# Revit family: 2Incepa_Boss_Bacia com Caixa Acoplar_89351
name_source: partatom
category: Plumbing Fixtures
revit_build: Autodesk Revit MEP 2014 (Build: 20131024_2115(x64)
units: mm (PartAtom-declared; Revit-internal decimal feet)

## types (2) — shared parameters
Assembly Code = D2010100
CWFU = 1
Description = Bacia com caixa acoplada cor branca (89351) 365 x 640 mm, linha Boss - Louças Incepa
Desenvolvido por = ofcdesk
Diâmetro Ponto de Esgoto = 100 mm
Incepa: Categoria = Linha Boss
Incepa: Cores Disponíveis = Branco
Incepa: Código = 89351
Incepa: Descrição = Bacia com caixa acoplada cor branca (89351) 365 x 640 mm, linha Boss - Louças Incepa
Incepa: Desenho Técnico = http://www.banheirosincepa.com.br
Incepa: Fabricante = Incepa
Incepa: Linha = Boss
Incepa: Link do Produto = http://www.banheirosincepa.com.br
Incepa: Norma = ABNT NBR 15097-1:2011/ABNT NBR 15097-2:2011 - fabricação/instalação
Incepa: Produto = Louças
Incepa: Tipo = Bacias com caixas
Incepa: Versão = Autodesk Revit MEP 2014
Manufacturer = Incepa
Model = 89351
Raio Ponto de Esgoto = 50 mm
Raio Ponto de Água = 10 mm
Selo de Qualidade ofcdesk = Standard
Tipo de caixa = Incepa_Boss_Caixa Acoplar_89570 : 01 - Branco
URL = http://www.logasa.com.br
WFU = 3
zero-valued in all types: Default Elevation

## per-type parameters (varying)
| type | Tipo de assento |
| 01 - Branco (Assento PP Boss) | Incepa_Assento PP Boss para Bacia Sanitária_89981 : 01 - Branco |
| 01 - Branco (Assento Boss Softclose) | Incepa_Assento PP Boss Softclose para Bacia Sanitária_89981 : 01 - Branco |

## geometry (parser evidence)
native form markers: Blend x4, Sweep x10
no freeform markers — native parametric forms only
